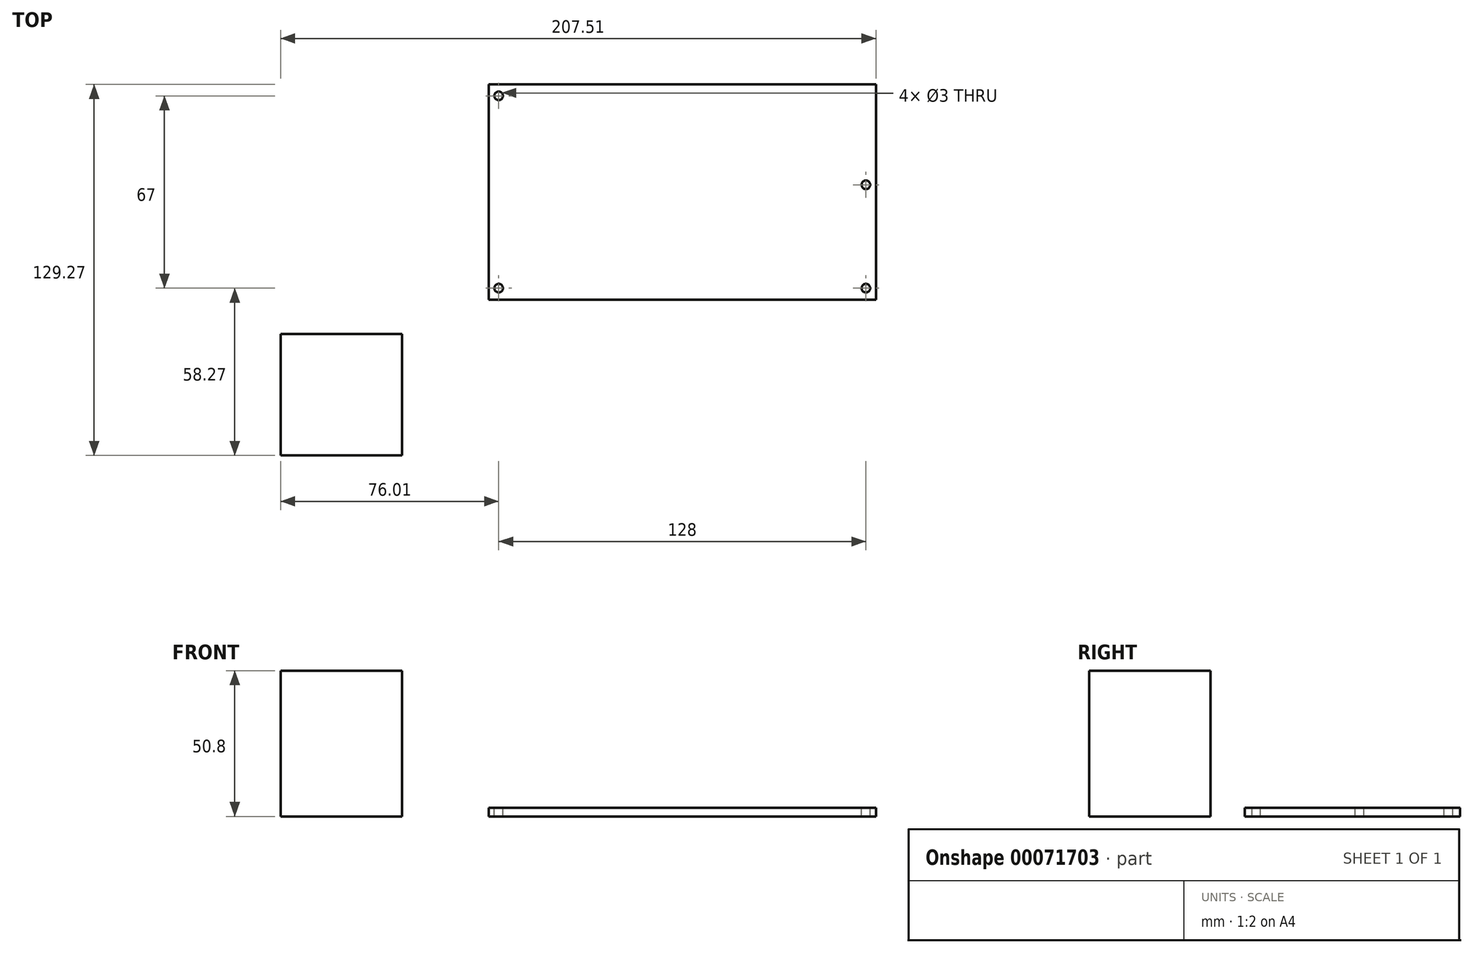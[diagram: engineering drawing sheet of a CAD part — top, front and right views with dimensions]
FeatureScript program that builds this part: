
annotation { "Feature Type Name" : "Feature", "Feature Type Description" : "" }
export const myFeature = defineFeature(function(context is Context, id is Id, definition is map)
    precondition{}
    {
        {
            var Q0;
            Q0=qCreatedBy(makeId("Top.planeOp"),FACE);
            var sketch = newSketch(context, id + "F0", { "sketchPlane" : qUnion([Q0])});
            skLineSegment(sketch, "E0.bottom", {"start": v(0, 0) * mm, "end": v(135, 0) * mm});
            skLineSegment(sketch, "E0.top", {"start": v(0, 75) * mm, "end": v(135, 75) * mm});
            skLineSegment(sketch, "E0.left", {"start": v(0, 0) * mm, "end": v(0, 75) * mm});
            skLineSegment(sketch, "E0.right", {"start": v(135, 0) * mm, "end": v(135, 75) * mm});
            skSolve(sketch);
        }
        {
            var Q0;
            Q0=makeQuery(id+"F0.imprint","IMPRINT",FACE,{"disambiguationData":[TD([[makeQuery(id+"F0.imprint","IMPRINT",EDGE,{"derivedFrom":sQuery(id+"F0.wireOp",EDGE,"E0.bottom")}),1.0]])]});
            extrude(context, id + "F1", {"entities" : qUnion([Q0]), "depth" : 3 * mm});
        }
        {
            var Q0;
            Q0=makeQuery(id+"F1.opExtrude","CAP_FACE",FACE,{"disambiguationData":[OSD([sQuery(id+"F0.wireOp",EDGE,"E0.bottom"),sQuery(id+"F0.wireOp",EDGE,"E0.top"),sQuery(id+"F0.wireOp",EDGE,"E0.left"),sQuery(id+"F0.wireOp",EDGE,"E0.right")])],"isStart":false});
            var sketch = newSketch(context, id + "F2", { "sketchPlane" : qUnion([Q0])});
            skCircle(sketch, "E1", {"center": v(3.5, 71) * mm, "radius": 1.5 * mm});
            skCircle(sketch, "E2", {"center": v(3.5, 4) * mm, "radius": 1.5 * mm});
            skCircle(sketch, "E3", {"center": v(131.5, 4) * mm, "radius": 1.5 * mm});
            skCircle(sketch, "E4", {"center": v(131.5, 40) * mm, "radius": 1.5 * mm});
            skSolve(sketch);
        }
        {
            var Q0;
            Q0 = qSketchRegion(id + "F2", true);
            extrude(context, id + "F3", {"entities" : qUnion([Q0]), "operationType" : NewBodyOperationType.REMOVE, "oppositeDirection" : true, "depth" : 25 * mm});
        }
        {
            var Q0;
            Q0=qCreatedBy(makeId("Top.planeOp"),FACE);
            var sketch = newSketch(context, id + "F4", { "sketchPlane" : qUnion([Q0])});
            skLineSegment(sketch, "E5.bottom", {"start": v(-72.51, -54.27) * mm, "end": v(-30.21, -54.27) * mm});
            skLineSegment(sketch, "E5.top", {"start": v(-72.51, -11.97) * mm, "end": v(-30.21, -11.97) * mm});
            skLineSegment(sketch, "E5.left", {"start": v(-72.51, -54.27) * mm, "end": v(-72.51, -11.97) * mm});
            skLineSegment(sketch, "E5.right", {"start": v(-30.21, -54.27) * mm, "end": v(-30.21, -11.97) * mm});
            skSolve(sketch);
        }
        {
            var Q0;
            Q0=makeQuery(id+"F4.imprint","IMPRINT",FACE,{"disambiguationData":[TD([[makeQuery(id+"F4.imprint","IMPRINT",EDGE,{"derivedFrom":sQuery(id+"F4.wireOp",EDGE,"E5.bottom")}),1.0]])]});
            extrude(context, id + "F5", {"entities" : qUnion([Q0]), "depth" : 50.8 * mm});
        }
    });
